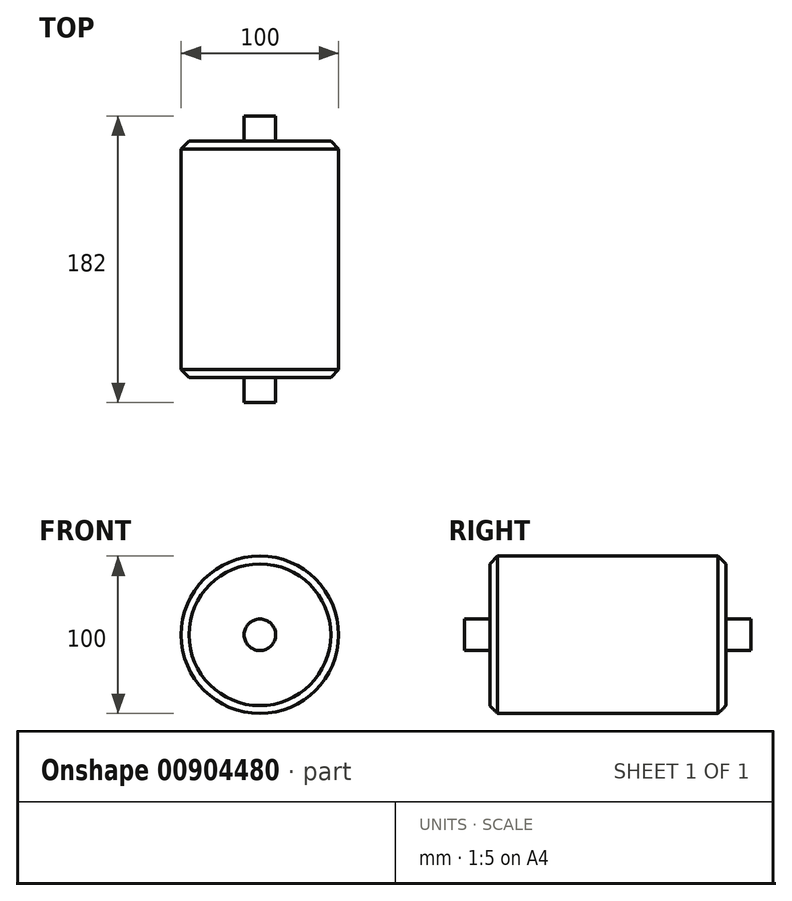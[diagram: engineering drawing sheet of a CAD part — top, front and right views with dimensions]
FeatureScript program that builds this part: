
annotation { "Feature Type Name" : "Feature", "Feature Type Description" : "" }
export const myFeature = defineFeature(function(context is Context, id is Id, definition is map)
    precondition{}
    {
        {
            var Q0;
            Q0=qCreatedBy(makeId("Front.planeOp"),FACE);
            var sketch = newSketch(context, id + "F0", { "sketchPlane" : qUnion([Q0])});
            skCircle(sketch, "E0", {"center": v(0, 0) * mm, "radius": 50 * mm});
            skSolve(sketch);
        }
        {
            var Q0;
            Q0=makeQuery(id+"F0.imprint","IMPRINT",FACE,{"disambiguationData":[TD([[makeQuery(id+"F0.imprint","IMPRINT",EDGE,{"derivedFrom":sQuery(id+"F0.wireOp",EDGE,"E0")}),1.0]])]});
            extrude(context, id + "F1", {"entities" : qUnion([Q0]), "depth" : 150 * mm, "offsetDistance" : 25.4 * mm});
        }
        {
            var Q0;
            Q0=makeQuery(id+"F1.opExtrude","CAP_FACE",FACE,{"disambiguationData":[OSD([sQuery(id+"F0.wireOp",EDGE,"E0")])],"isStart":false});
            var sketch = newSketch(context, id + "F2", { "sketchPlane" : qUnion([Q0])});
            skCircle(sketch, "E1", {"center": v(0, 0) * mm, "radius": 10 * mm});
            skSolve(sketch);
        }
        {
            var Q0;
            Q0=makeQuery(id+"F2.imprint","IMPRINT",FACE,{"disambiguationData":[TD([[makeQuery(id+"F2.imprint","IMPRINT",EDGE,{"derivedFrom":sQuery(id+"F2.wireOp",EDGE,"E1")}),1.0]])]});
            extrude(context, id + "F3", {"entities" : qUnion([Q0]), "operationType" : NewBodyOperationType.ADD, "depth" : 16 * mm, "offsetDistance" : 25.4 * mm});
        }
        {
            var Q0;
            Q0=makeQuery(id+"F0.imprint","IMPRINT",FACE,{"disambiguationData":[TD([[makeQuery(id+"F0.imprint","IMPRINT",EDGE,{"derivedFrom":sQuery(id+"F0.wireOp",EDGE,"E0")}),1.0]])]});
            var sketch = newSketch(context, id + "F4", { "sketchPlane" : qUnion([Q0])});
            skCircle(sketch, "E2", {"center": v(0, 0) * mm, "radius": 10 * mm});
            skSolve(sketch);
        }
        {
            var Q0;
            Q0=makeQuery(id+"F4.imprint","IMPRINT",FACE,{"disambiguationData":[TD([[makeQuery(id+"F4.imprint","IMPRINT",EDGE,{"derivedFrom":sQuery(id+"F4.wireOp",EDGE,"E2")}),1.0]])]});
            extrude(context, id + "F5", {"entities" : qUnion([Q0]), "operationType" : NewBodyOperationType.ADD, "oppositeDirection" : true, "depth" : 16 * mm, "offsetDistance" : 25.4 * mm});
        }
        {
            var Q0;
            Q0=makeQuery(id+"F1.opExtrude","CAP_EDGE",EDGE,{"disambiguationData":[OSD([sQuery(id+"F0.wireOp",EDGE,"E0")])],"isStart":true});
            chamfer(context, id + "F6", {"entities" : qUnion([Q0]), "width" : 5 * mm, "tangentPropagation" : true});
        }
        {
            var Q0;
            Q0=makeQuery(id+"F1.opExtrude","CAP_EDGE",EDGE,{"disambiguationData":[OSD([sQuery(id+"F0.wireOp",EDGE,"E0")])],"isStart":false});
            chamfer(context, id + "F7", {"entities" : qUnion([Q0]), "width" : 5 * mm, "tangentPropagation" : true});
        }
    });
